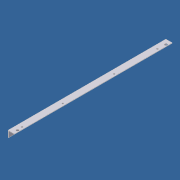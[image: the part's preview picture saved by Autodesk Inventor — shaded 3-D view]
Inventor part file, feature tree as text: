
AUTODESK INVENTOR PART (.ipt)
format: ipt  version: unknown  size: 177,664 bytes
history: native  units: in
note: dims shown in document units (in); Inventor stores cm internally (conversion verified against a paired STEP export)
features: hole x6, extrude x1, sketch x1
ambient origin geometry x8: Origin, YZ Plane, XZ Plane, XY Plane, X Axis, Y Axis, Z Axis, Center Point
feature tree (8):
  extrude  "Extrusion1"  Depth=2.0in
  hole  "Hole1"  [1 undecoded]
  hole  "Hole2"  [1 undecoded]
  hole  "Hole3"  [1 undecoded]
  hole  "Hole4"  [1 undecoded]
  hole  "Hole5"  [1 undecoded]
  hole  "Hole6"  [1 undecoded]
  sketch  "Sketch1"  dims[d0=2.0in d1=2.0in d2=0.125in d4=0.125in d5=49.1875in d6=0.0in d7=1.4688in d8=1.5in d9=0.8125in d10=0.5in d11=0.375in d12=0.25in d13=0.5635in d14=0.75in d15=0.8108in d16=3.0625in d17=1.3125in d18=0.5625in d19=0.5in d20=0.375in d21=0.25in d22=0.5635in d23=0.75in d24=0.8108in d25=15.75in d26=1.3125in d27=0.5625in d28=0.5in d29=0.375in d30=0.25in d31=0.5635in d32=0.75in d33=0.8108in d34=31.75in d35=1.3125in d36=0.5625in d37=0.5in d38=0.375in d39=0.25in d40=0.5635in d41=0.75in d42=0.8108in d43=45.25in d44=1.3125in d45=0.5625in d46=0.5in d47=0.375in d48=0.25in d49=0.5635in d50=0.75in d51=0.8108in d52=1.4688in d53=1.5in d54=0.8125in d55=0.5in d56=0.375in d57=0.25in d58=0.5635in d59=0.75in d60=0.8108in]
note: 6 required parameter values undecoded (feature->parameter linkage not recoverable at this tier; creation-order binding heuristic only, values carry confidence <= 0.55)
